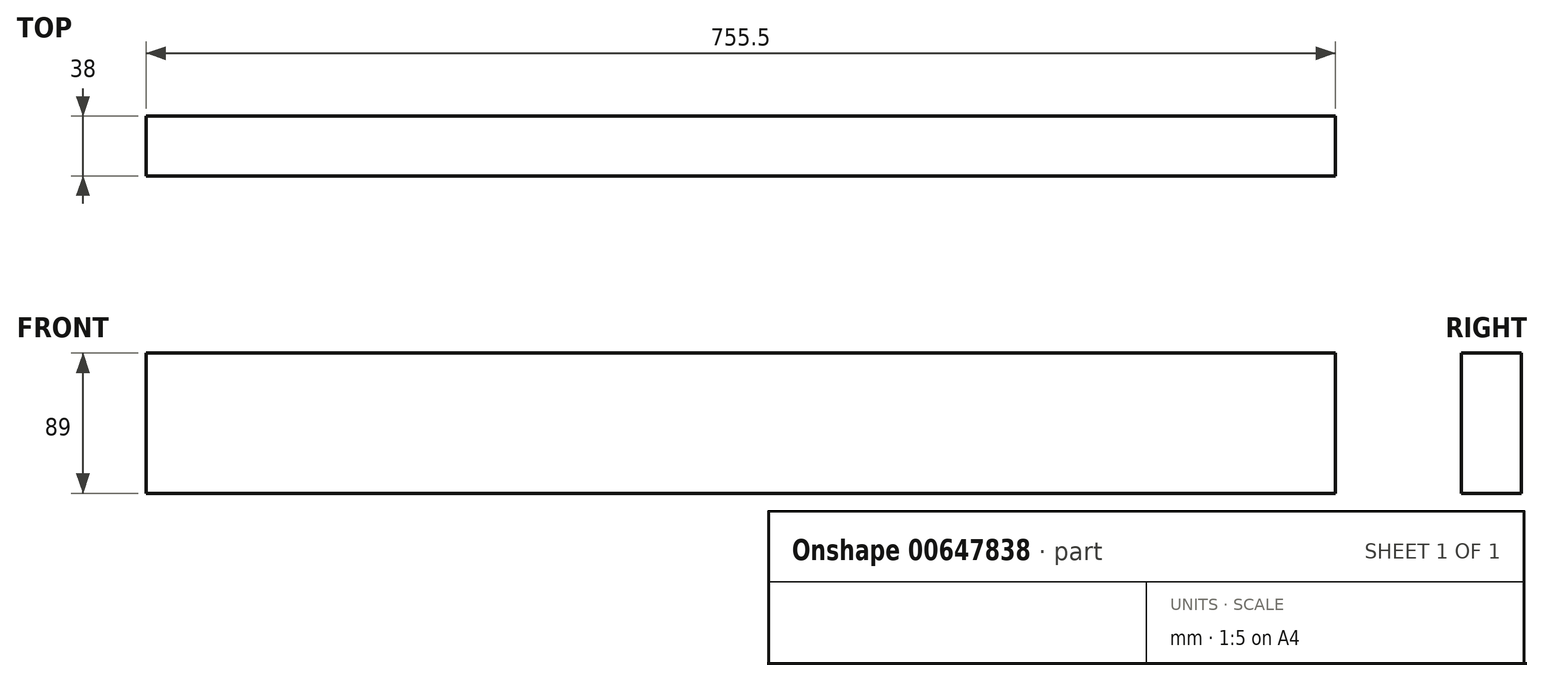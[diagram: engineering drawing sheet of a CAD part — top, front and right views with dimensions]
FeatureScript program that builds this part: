
annotation { "Feature Type Name" : "Feature", "Feature Type Description" : "" }
export const myFeature = defineFeature(function(context is Context, id is Id, definition is map)
    precondition{}
    {
        {
            var Q0;
            Q0=qCreatedBy(makeId("Front.planeOp"),FACE);
            var sketch = newSketch(context, id + "F0", { "sketchPlane" : qUnion([Q0])});
            skLineSegment(sketch, "E0.bottom", {"start": v(-377.75, -44.5) * mm, "end": v(377.75, -44.5) * mm});
            skLineSegment(sketch, "E0.top", {"start": v(-377.75, 44.5) * mm, "end": v(377.75, 44.5) * mm});
            skLineSegment(sketch, "E0.left", {"start": v(-377.75, -44.5) * mm, "end": v(-377.75, 44.5) * mm});
            skLineSegment(sketch, "E0.right", {"start": v(377.75, -44.5) * mm, "end": v(377.75, 44.5) * mm});
            skPoint(sketch, "E0.middle", {"position": v(0, 0) * mm});
            skSolve(sketch);
        }
        {
            var Q0;
            Q0 = qSketchRegion(id + "F0", true);
            extrude(context, id + "F1", {"entities" : qUnion([Q0]), "depth" : 38 * mm, "offsetDistance" : 25 * mm});
        }
    });
